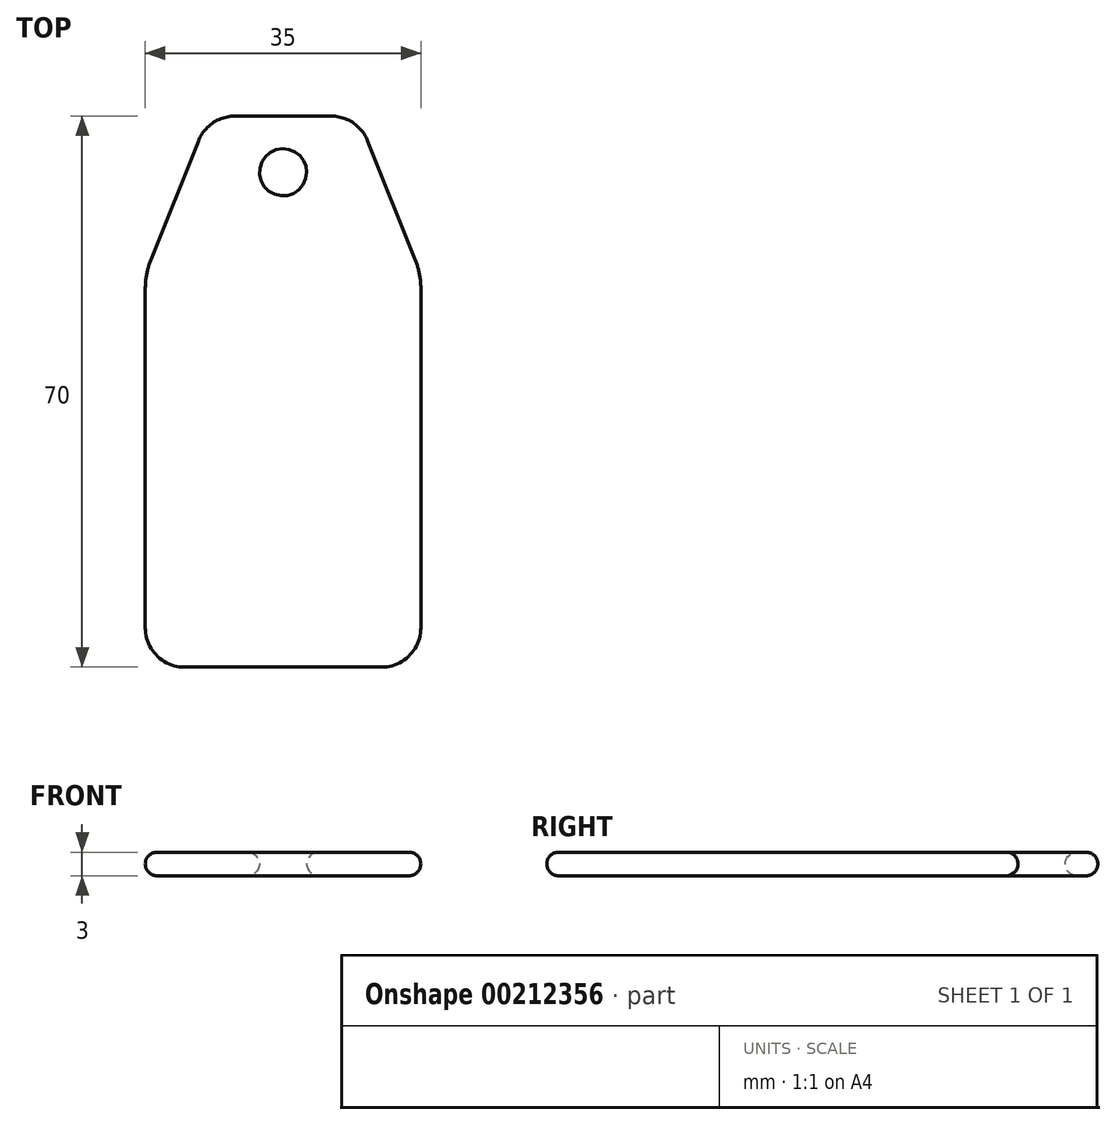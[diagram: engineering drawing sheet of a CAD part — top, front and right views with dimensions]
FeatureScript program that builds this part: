
annotation { "Feature Type Name" : "Feature", "Feature Type Description" : "" }
export const myFeature = defineFeature(function(context is Context, id is Id, definition is map)
    precondition{}
    {
        {
            var Q0;
            Q0=qCreatedBy(makeId("Top.planeOp"),FACE);
            var sketch = newSketch(context, id + "F0", { "sketchPlane" : qUnion([Q0])});
            skLineSegment(sketch, "E0.bottom", {"start": v(-12.5, -35) * mm, "end": v(12.5, -35) * mm});
            skLineSegment(sketch, "E0.top", {"start": v(-6.11, 35) * mm, "end": v(6.11, 35) * mm});
            skLineSegment(sketch, "E0.left", {"start": v(-17.5, -30) * mm, "end": v(-17.5, 13.07) * mm});
            skLineSegment(sketch, "E0.right", {"start": v(17.5, -30) * mm, "end": v(17.5, 13.07) * mm});
            skPoint(sketch, "E0.middle", {"position": v(0, 0) * mm});
            skLineSegment(sketch, "E1", {"start": v(-16.78, 16.79) * mm, "end": v(-10.76, 31.86) * mm});
            skLineSegment(sketch, "E2", {"start": v(16.78, 16.79) * mm, "end": v(10.76, 31.86) * mm});
            skPoint(sketch, "E3.orphan", {"position": v(-17.5, 35) * mm});
            skPoint(sketch, "E4.orphan", {"position": v(17.5, 35) * mm});
            skPoint(sketch, "E5", {"position": v(0, 27.87) * mm});
            skCircle(sketch, "E6", {"center": v(0, 27.87) * mm, "radius": 3 * mm});
            skPoint(sketch, "E7.visualSharp", {"position": v(-17.5, 15) * mm});
            skArc(sketch, "E7.filletArc", {"start": v(-16.78, 16.79) * mm, "mid": v(-17.32, 14.97) * mm, "end": v(-17.5, 13.07) * mm});
            skPoint(sketch, "E8.visualSharp", {"position": v(17.5, 15) * mm});
            skArc(sketch, "E8.filletArc", {"start": v(17.5, 13.07) * mm, "mid": v(17.32, 14.97) * mm, "end": v(16.78, 16.79) * mm});
            skPoint(sketch, "E9.visualSharp", {"position": v(-9.5, 35) * mm});
            skArc(sketch, "E9.filletArc", {"start": v(-6.11, 35) * mm, "mid": v(-8.92, 34.14) * mm, "end": v(-10.76, 31.86) * mm});
            skPoint(sketch, "E10.visualSharp", {"position": v(9.5, 35) * mm});
            skArc(sketch, "E10.filletArc", {"start": v(10.76, 31.86) * mm, "mid": v(8.92, 34.14) * mm, "end": v(6.11, 35) * mm});
            skPoint(sketch, "E11.visualSharp", {"position": v(-17.5, -35) * mm});
            skArc(sketch, "E11.filletArc", {"start": v(-17.5, -30) * mm, "mid": v(-16.04, -33.54) * mm, "end": v(-12.5, -35) * mm});
            skPoint(sketch, "E12.visualSharp", {"position": v(17.5, -35) * mm});
            skArc(sketch, "E12.filletArc", {"start": v(12.5, -35) * mm, "mid": v(16.04, -33.54) * mm, "end": v(17.5, -30) * mm});
            skSolve(sketch);
        }
        {
            var Q0;
            Q0 = qSketchRegion(id + "F0", true);
            extrude(context, id + "F1", {"entities" : qUnion([Q0]), "depth" : 3 * mm});
        }
        {
            var Q0;
            Q0=makeQuery(id+"F1.opExtrude","CAP_FACE",FACE,{"disambiguationData":[OSD([sQuery(id+"F0.wireOp",EDGE,"E0.bottom"),sQuery(id+"F0.wireOp",EDGE,"E0.top"),sQuery(id+"F0.wireOp",EDGE,"E0.left"),sQuery(id+"F0.wireOp",EDGE,"E0.right"),sQuery(id+"F0.wireOp",EDGE,"E1"),sQuery(id+"F0.wireOp",EDGE,"E2"),sQuery(id+"F0.wireOp",EDGE,"E6"),sQuery(id+"F0.wireOp",EDGE,"E7.filletArc"),sQuery(id+"F0.wireOp",EDGE,"E8.filletArc"),sQuery(id+"F0.wireOp",EDGE,"E9.filletArc"),sQuery(id+"F0.wireOp",EDGE,"E10.filletArc"),sQuery(id+"F0.wireOp",EDGE,"E11.filletArc"),sQuery(id+"F0.wireOp",EDGE,"E12.filletArc")])],"isStart":false});
            var Q1;
            Q1=makeQuery(id+"F1.opExtrude","CAP_FACE",FACE,{"disambiguationData":[OSD([sQuery(id+"F0.wireOp",EDGE,"E0.bottom"),sQuery(id+"F0.wireOp",EDGE,"E0.top"),sQuery(id+"F0.wireOp",EDGE,"E0.left"),sQuery(id+"F0.wireOp",EDGE,"E0.right"),sQuery(id+"F0.wireOp",EDGE,"E1"),sQuery(id+"F0.wireOp",EDGE,"E2"),sQuery(id+"F0.wireOp",EDGE,"E6"),sQuery(id+"F0.wireOp",EDGE,"E7.filletArc"),sQuery(id+"F0.wireOp",EDGE,"E8.filletArc"),sQuery(id+"F0.wireOp",EDGE,"E9.filletArc"),sQuery(id+"F0.wireOp",EDGE,"E10.filletArc"),sQuery(id+"F0.wireOp",EDGE,"E11.filletArc"),sQuery(id+"F0.wireOp",EDGE,"E12.filletArc")])],"isStart":true});
            fillet(context, id + "F2", {"entities" : qUnion([Q0, Q1]), "radius" : 1.5 * mm, "tangentPropagation" : true, "allowEdgeOverflow" : false});
        }
    });
